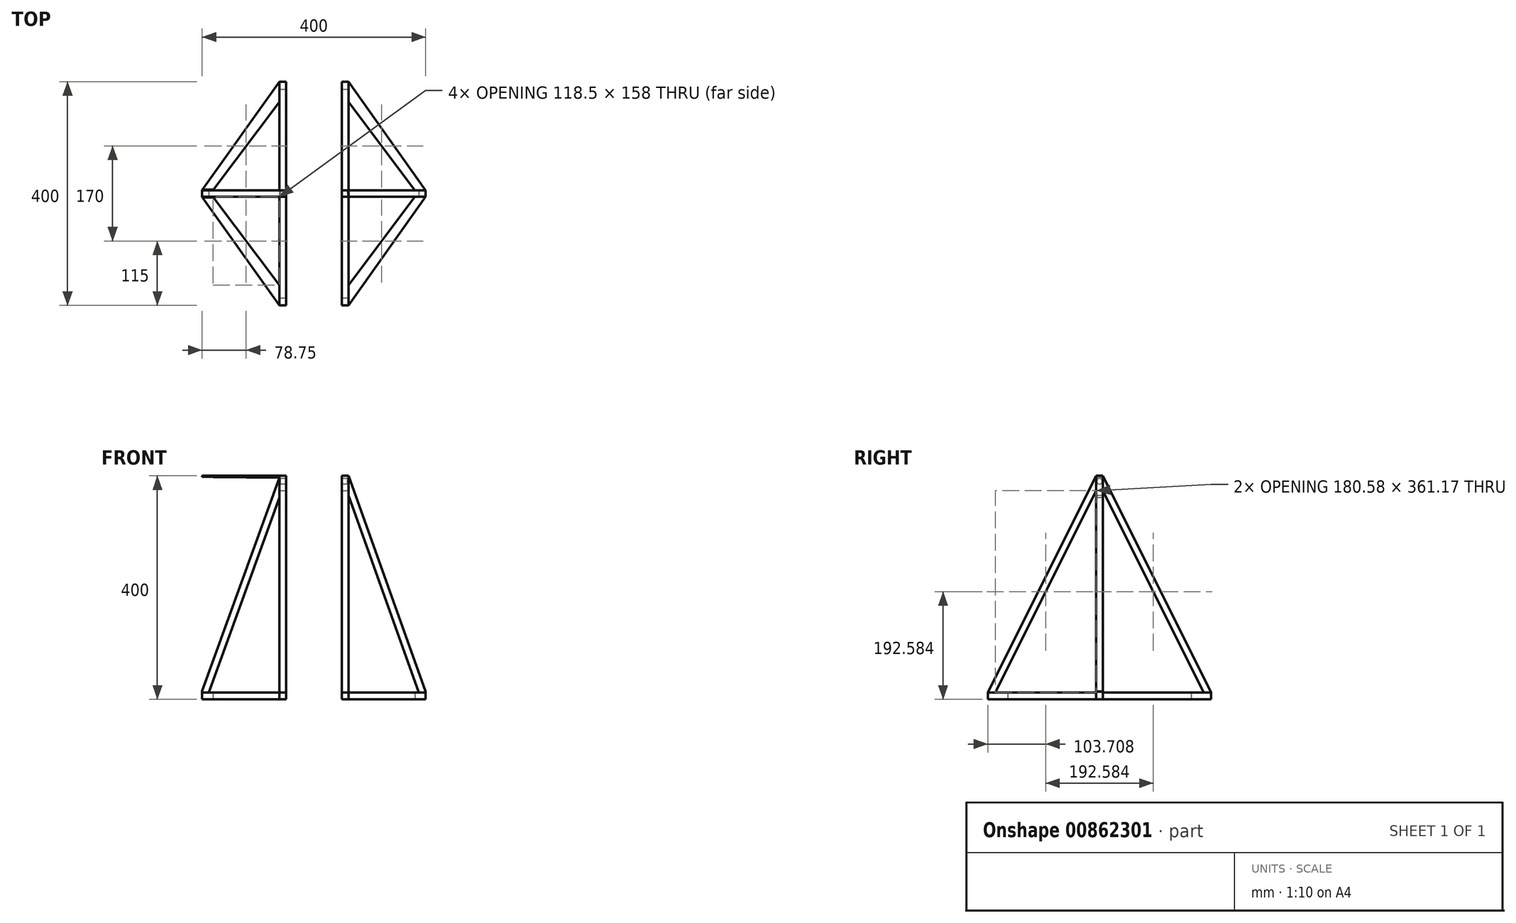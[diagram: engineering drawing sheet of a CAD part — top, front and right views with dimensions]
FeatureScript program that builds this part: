
annotation { "Feature Type Name" : "Feature", "Feature Type Description" : "" }
export const myFeature = defineFeature(function(context is Context, id is Id, definition is map)
    precondition{}
    {
        {
            var Q0;
            Q0=qCreatedBy(makeId("Top.planeOp"),FACE);
            cPlane(context, id + "F0", {"entities" : qUnion([Q0]), "cplaneType" : CPlaneType.OFFSET, "offset" : 141 * mm, "width" : 150 * mm, "height" : 150 * mm});
        }
        {
            var Q0;
            Q0=qCreatedBy(makeId("Top.planeOp"),FACE);
            var sketch = newSketch(context, id + "F1", { "sketchPlane" : qUnion([Q0])});
            skLineSegment(sketch, "E0.bottom", {"start": v(-40, 200) * mm, "end": v(40, 200) * mm, "construction": true});
            skLineSegment(sketch, "E0.top", {"start": v(-40, -200) * mm, "end": v(40, -200) * mm, "construction": true});
            skPoint(sketch, "E0.middle", {"position": v(0, 0) * mm});
            skLineSegment(sketch, "E1", {"start": v(-200, 0) * mm, "end": v(200, 0) * mm, "construction": true});
            skLineSegment(sketch, "E2.bottom", {"start": v(-50, 200) * mm, "end": v(50, 200) * mm, "construction": true});
            skLineSegment(sketch, "E2.top", {"start": v(-50, -200) * mm, "end": v(50, -200) * mm, "construction": true});
            skLineSegment(sketch, "E2.left", {"start": v(-50, 200) * mm, "end": v(-50, -200) * mm, "construction": true});
            skLineSegment(sketch, "E2.right", {"start": v(50, 200) * mm, "end": v(50, -200) * mm, "construction": true});
            skLineSegment(sketch, "E3.bottom", {"start": v(-200, 6) * mm, "end": v(200, 6) * mm, "construction": true});
            skLineSegment(sketch, "E3.top", {"start": v(-200, -6) * mm, "end": v(200, -6) * mm, "construction": true});
            skLineSegment(sketch, "E3.left", {"start": v(-200, 6) * mm, "end": v(-200, -6) * mm, "construction": true});
            skLineSegment(sketch, "E3.right", {"start": v(200, 6) * mm, "end": v(200, -6) * mm, "construction": true});
            skLineSegment(sketch, "E4", {"start": v(-200, 6) * mm, "end": v(-200, -6) * mm});
            skLineSegment(sketch, "E5.bottom", {"start": v(-50, 200) * mm, "end": v(-62, 200) * mm, "construction": true});
            skLineSegment(sketch, "E5.top", {"start": v(-50, -200) * mm, "end": v(-62, -200) * mm, "construction": true});
            skLineSegment(sketch, "E5.right", {"start": v(-62, 200) * mm, "end": v(-62, -200) * mm, "construction": true});
            skLineSegment(sketch, "E6", {"start": v(0, -95.75) * mm, "end": v(0, 160.13) * mm, "construction": true});
            skPoint(sketch, "E6.endSnap0", {"position": v(0, -6) * mm});
            skLineSegment(sketch, "E7.bottom", {"start": v(50, 200) * mm, "end": v(62, 200) * mm, "construction": true});
            skLineSegment(sketch, "E7.top", {"start": v(50, -200) * mm, "end": v(62, -200) * mm, "construction": true});
            skLineSegment(sketch, "E7.right", {"start": v(62, 200) * mm, "end": v(62, -200) * mm, "construction": true});
            skLineSegment(sketch, "E8", {"start": v(-62, 200) * mm, "end": v(-200, 6) * mm});
            skLineSegment(sketch, "E9", {"start": v(-62, 200) * mm, "end": v(-50, 200) * mm});
            skLineSegment(sketch, "E10", {"start": v(-50, 200) * mm, "end": v(-50, -200) * mm});
            skLineSegment(sketch, "E11", {"start": v(-50, -200) * mm, "end": v(-62, -200) * mm});
            skLineSegment(sketch, "E12", {"start": v(-62, -200) * mm, "end": v(-200, -6) * mm});
            skLineSegment(sketch, "E13", {"start": v(50, 200) * mm, "end": v(62, 200) * mm});
            skLineSegment(sketch, "E14", {"start": v(62, 200) * mm, "end": v(200, 6) * mm});
            skLineSegment(sketch, "E15", {"start": v(200, 6) * mm, "end": v(200, -6) * mm});
            skLineSegment(sketch, "E16", {"start": v(200, -6) * mm, "end": v(62, -200) * mm});
            skLineSegment(sketch, "E17", {"start": v(62, -200) * mm, "end": v(50, -200) * mm});
            skLineSegment(sketch, "E18", {"start": v(50, -200) * mm, "end": v(50, 200) * mm});
            skSolve(sketch);
        }
        {
            var Q0;
            Q0 = qSketchRegion(id + "F1", true);
            extrude(context, id + "F2", {"entities" : qUnion([Q0]), "depth" : 400 * mm, "offsetDistance" : 25 * mm});
        }
        {
            var Q0;
            Q0=qCreatedBy(makeId("Front.planeOp"),FACE);
            var sketch = newSketch(context, id + "F3", { "sketchPlane" : qUnion([Q0])});
            skLineSegment(sketch, "E19.bottom", {"start": v(50, 0) * mm, "end": v(-50, 0) * mm, "construction": true});
            skLineSegment(sketch, "E19.top", {"start": v(50, 400) * mm, "end": v(-48.58, 400) * mm, "construction": true});
            skLineSegment(sketch, "E20", {"start": v(-200, 15) * mm, "end": v(-62, 396.08) * mm});
            skLineSegment(sketch, "E21", {"start": v(-62, 360.83) * mm, "end": v(-188.32, 12) * mm});
            skLineSegment(sketch, "E22", {"start": v(-188.32, 12) * mm, "end": v(-62, 12) * mm});
            skLineSegment(sketch, "E23", {"start": v(-62, 12) * mm, "end": v(-62, 360.83) * mm});
            skLineSegment(sketch, "E24.bottom", {"start": v(-50, 0) * mm, "end": v(-340.13, 0) * mm, "construction": true});
            skLineSegment(sketch, "E24.top", {"start": v(-50, 400) * mm, "end": v(-340.13, 400) * mm, "construction": true});
            skLineSegment(sketch, "E24.left", {"start": v(-50, 0) * mm, "end": v(-50, 400) * mm, "construction": true});
            skLineSegment(sketch, "E24.right", {"start": v(-340.13, 0) * mm, "end": v(-340.13, 400) * mm, "construction": true});
            skLineSegment(sketch, "E25", {"start": v(-62, 396.08) * mm, "end": v(-340.13, 400) * mm});
            skLineSegment(sketch, "E26", {"start": v(-340.13, 400) * mm, "end": v(-200, 15) * mm});
            skLineSegment(sketch, "E27.left", {"start": v(50, 0) * mm, "end": v(50, 400) * mm, "construction": true});
            skSolve(sketch);
        }
        {
            var Q0;
            Q0 = qSketchRegion(id + "F3", true);
            extrude(context, id + "F4", {"entities" : qUnion([Q0]), "operationType" : NewBodyOperationType.REMOVE, "endBound" : BoundingType.SYMMETRIC, "oppositeDirection" : true, "depth" : 1000 * mm, "offsetDistance" : 25 * mm});
        }
        {
            var Q0;
            Q0=qCreatedBy(makeId("Front.planeOp"),FACE);
            var sketch = newSketch(context, id + "F5", { "sketchPlane" : qUnion([Q0])});
            skLineSegment(sketch, "E28.bottom", {"start": v(50, 0) * mm, "end": v(-50, 0) * mm, "construction": true});
            skLineSegment(sketch, "E28.top", {"start": v(50, 400) * mm, "end": v(-50, 400) * mm, "construction": true});
            skLineSegment(sketch, "E28.left", {"start": v(50, 0) * mm, "end": v(50, 400) * mm, "construction": true});
            skLineSegment(sketch, "E28.right", {"start": v(-50, 0) * mm, "end": v(-50, 400) * mm, "construction": true});
            skLineSegment(sketch, "E29.bottom", {"start": v(50, 0) * mm, "end": v(200, 0) * mm, "construction": true});
            skLineSegment(sketch, "E30", {"start": v(62, 364.36) * mm, "end": v(62, 12) * mm});
            skLineSegment(sketch, "E31", {"start": v(188, 12) * mm, "end": v(62, 364.36) * mm});
            skLineSegment(sketch, "E32", {"start": v(62, 12) * mm, "end": v(188, 12) * mm});
            skLineSegment(sketch, "E33", {"start": v(62, 400) * mm, "end": v(200, 14.08) * mm});
            skLineSegment(sketch, "E34", {"start": v(200, 14.08) * mm, "end": v(200, 400) * mm});
            skLineSegment(sketch, "E35", {"start": v(62, 400) * mm, "end": v(200, 400) * mm});
            skSolve(sketch);
        }
        {
            var Q0;
            Q0 = qSketchRegion(id + "F5", true);
            extrude(context, id + "F6", {"entities" : qUnion([Q0]), "operationType" : NewBodyOperationType.REMOVE, "endBound" : BoundingType.SYMMETRIC, "oppositeDirection" : true, "depth" : 1000 * mm, "offsetDistance" : 25 * mm});
        }
        {
            var Q0;
            Q0=qCreatedBy(makeId("Right.planeOp"),FACE);
            var sketch = newSketch(context, id + "F7", { "sketchPlane" : qUnion([Q0])});
            skLineSegment(sketch, "E36.bottom", {"start": v(200, 0) * mm, "end": v(-200, 0) * mm, "construction": true});
            skLineSegment(sketch, "E36.top", {"start": v(200, 400) * mm, "end": v(-200, 400) * mm, "construction": true});
            skLineSegment(sketch, "E36.left", {"start": v(200, 0) * mm, "end": v(200, 400) * mm, "construction": true});
            skLineSegment(sketch, "E36.right", {"start": v(-200, 0) * mm, "end": v(-200, 400) * mm, "construction": true});
            skLineSegment(sketch, "E37", {"start": v(-200, 400) * mm, "end": v(-200, 12) * mm});
            skLineSegment(sketch, "E38", {"start": v(-200, 12) * mm, "end": v(-6, 400) * mm});
            skLineSegment(sketch, "E39", {"start": v(-6, 400) * mm, "end": v(-200, 400) * mm});
            skLineSegment(sketch, "E40", {"start": v(0, 0) * mm, "end": v(0, 400) * mm, "construction": true});
            skLineSegment(sketch, "E41", {"start": v(200, 400) * mm, "end": v(200, 12) * mm});
            skLineSegment(sketch, "E42", {"start": v(200, 12) * mm, "end": v(6, 400) * mm});
            skLineSegment(sketch, "E43", {"start": v(6, 400) * mm, "end": v(200, 400) * mm});
            skLineSegment(sketch, "E44.bottom", {"start": v(-200, 0) * mm, "end": v(200, 0) * mm, "construction": true});
            skLineSegment(sketch, "E44.top", {"start": v(-200, 12) * mm, "end": v(200, 12) * mm, "construction": true});
            skLineSegment(sketch, "E44.left", {"start": v(-200, 0) * mm, "end": v(-200, 12) * mm, "construction": true});
            skLineSegment(sketch, "E44.right", {"start": v(200, 0) * mm, "end": v(200, 12) * mm, "construction": true});
            skLineSegment(sketch, "E45", {"start": v(-186.58, 12) * mm, "end": v(-6, 373.17) * mm});
            skLineSegment(sketch, "E46", {"start": v(-6, 373.17) * mm, "end": v(-6, 12) * mm});
            skLineSegment(sketch, "E47", {"start": v(-6, 12) * mm, "end": v(-186.58, 12) * mm});
            skLineSegment(sketch, "E48", {"start": v(186.58, 12) * mm, "end": v(6, 373.17) * mm});
            skLineSegment(sketch, "E49", {"start": v(6, 373.17) * mm, "end": v(6, 12) * mm});
            skLineSegment(sketch, "E50", {"start": v(6, 12) * mm, "end": v(186.58, 12) * mm});
            skSolve(sketch);
        }
        {
            var Q0;
            Q0 = qSketchRegion(id + "F7", true);
            extrude(context, id + "F8", {"entities" : qUnion([Q0]), "operationType" : NewBodyOperationType.REMOVE, "endBound" : BoundingType.SYMMETRIC, "oppositeDirection" : true, "depth" : 400 * mm, "offsetDistance" : 25 * mm});
        }
        {
            var Q0;
            Q0=qCreatedBy(makeId("Top.planeOp"),FACE);
            var sketch = newSketch(context, id + "F9", { "sketchPlane" : qUnion([Q0])});
            skLineSegment(sketch, "E51.bottom", {"start": v(-50, 200) * mm, "end": v(50, 200) * mm, "construction": true});
            skLineSegment(sketch, "E51.top", {"start": v(-50, -200) * mm, "end": v(50, -200) * mm, "construction": true});
            skLineSegment(sketch, "E51.left", {"start": v(-50, 200) * mm, "end": v(-50, -200) * mm, "construction": true});
            skLineSegment(sketch, "E51.right", {"start": v(50, 200) * mm, "end": v(50, -200) * mm, "construction": true});
            skPoint(sketch, "E51.middle", {"position": v(0, 0) * mm});
            skLineSegment(sketch, "E52", {"start": v(0, 0) * mm, "end": v(200, 0) * mm, "construction": true});
            skLineSegment(sketch, "E53", {"start": v(50, 200) * mm, "end": v(200, 0) * mm, "construction": true});
            skLineSegment(sketch, "E54", {"start": v(50, 200) * mm, "end": v(50, 0) * mm, "construction": true});
            skLineSegment(sketch, "E55", {"start": v(180.5, 6) * mm, "end": v(62, 164) * mm});
            skLineSegment(sketch, "E56", {"start": v(62, 164) * mm, "end": v(62, 6) * mm});
            skLineSegment(sketch, "E57", {"start": v(62, 6) * mm, "end": v(180.5, 6) * mm});
            skLineSegment(sketch, "E58", {"start": v(50, -200) * mm, "end": v(200, 0) * mm, "construction": true});
            skLineSegment(sketch, "E59", {"start": v(62, -6) * mm, "end": v(62, -164) * mm});
            skLineSegment(sketch, "E60", {"start": v(62, -164) * mm, "end": v(180.5, -6) * mm});
            skLineSegment(sketch, "E61", {"start": v(180.5, -6) * mm, "end": v(62, -6) * mm});
            skLineSegment(sketch, "E62", {"start": v(0, 0) * mm, "end": v(0, 210) * mm, "construction": true});
            skLineSegment(sketch, "E63", {"start": v(-62, 164) * mm, "end": v(-62, 6) * mm});
            skLineSegment(sketch, "E64", {"start": v(-62, 6) * mm, "end": v(-180.5, 6) * mm});
            skLineSegment(sketch, "E65", {"start": v(-180.5, 6) * mm, "end": v(-62, 164) * mm});
            skLineSegment(sketch, "E66", {"start": v(-180.5, -6) * mm, "end": v(-62, -6) * mm});
            skLineSegment(sketch, "E67", {"start": v(-62, -6) * mm, "end": v(-62, -164) * mm});
            skLineSegment(sketch, "E68", {"start": v(-62, -164) * mm, "end": v(-180.5, -6) * mm});
            skSolve(sketch);
        }
        {
            var Q0;
            Q0 = qSketchRegion(id + "F9", true);
            extrude(context, id + "F10", {"entities" : qUnion([Q0]), "operationType" : NewBodyOperationType.REMOVE, "depth" : 400 * mm, "offsetDistance" : 25 * mm});
        }
        {
            var Q0;
            Q0=qCreatedBy(makeId("Right.planeOp"),FACE);
            var sketch = newSketch(context, id + "F11", { "sketchPlane" : qUnion([Q0])});
            skLineSegment(sketch, "E69", {"start": v(0, 0) * mm, "end": v(0, 390) * mm, "construction": true});
            skCircle(sketch, "E70", {"center": v(0, 390) * mm, "radius": 5 * mm});
            skSolve(sketch);
        }
        {
            var Q0;
            Q0 = qSketchRegion(id + "F11", true);
            extrude(context, id + "F12", {"entities" : qUnion([Q0]), "operationType" : NewBodyOperationType.REMOVE, "endBound" : BoundingType.SYMMETRIC, "depth" : 120 * mm, "offsetDistance" : 25 * mm});
        }
        {
            var Q0;
            Q0=qCreatedBy(id+"F0.planeOp",FACE);
            var sketch = newSketch(context, id + "F13", { "sketchPlane" : qUnion([Q0])});
            skLineSegment(sketch, "E71.bottom", {"start": v(-200, 6) * mm, "end": v(200, 6) * mm, "construction": true});
            skLineSegment(sketch, "E71.top", {"start": v(-200, -6) * mm, "end": v(200, -6) * mm, "construction": true});
            skLineSegment(sketch, "E71.left", {"start": v(-200, 6) * mm, "end": v(-200, -6) * mm, "construction": true});
            skLineSegment(sketch, "E71.right", {"start": v(200, 6) * mm, "end": v(200, -6) * mm, "construction": true});
            skPoint(sketch, "E71.middle", {"position": v(0, 0) * mm});
            skLineSegment(sketch, "E72.bottom", {"start": v(-62, 200) * mm, "end": v(62, 200) * mm, "construction": true});
            skLineSegment(sketch, "E72.top", {"start": v(-62, -200) * mm, "end": v(62, -200) * mm, "construction": true});
            skLineSegment(sketch, "E72.left", {"start": v(-62, 200) * mm, "end": v(-62, -200) * mm, "construction": true});
            skLineSegment(sketch, "E72.right", {"start": v(62, 200) * mm, "end": v(62, -200) * mm, "construction": true});
            skLineSegment(sketch, "E73", {"start": v(-62, -6) * mm, "end": v(-200, -6) * mm});
            skLineSegment(sketch, "E74", {"start": v(-200, -6) * mm, "end": v(-62, -200) * mm});
            skLineSegment(sketch, "E75", {"start": v(-62, -200) * mm, "end": v(-62, -6) * mm});
            skLineSegment(sketch, "E76", {"start": v(-62, 6) * mm, "end": v(-62, 200) * mm});
            skLineSegment(sketch, "E77", {"start": v(-62, 6) * mm, "end": v(-200, 6) * mm});
            skLineSegment(sketch, "E78", {"start": v(-200, 6) * mm, "end": v(-62, 200) * mm});
            skLineSegment(sketch, "E79", {"start": v(62, 6) * mm, "end": v(200, 6) * mm});
            skLineSegment(sketch, "E80", {"start": v(62, 6) * mm, "end": v(62, 200) * mm});
            skLineSegment(sketch, "E81", {"start": v(62, 200) * mm, "end": v(200, 6) * mm});
            skLineSegment(sketch, "E82", {"start": v(62, -6) * mm, "end": v(62, -200) * mm});
            skLineSegment(sketch, "E83", {"start": v(62, -6) * mm, "end": v(200, -6) * mm});
            skLineSegment(sketch, "E84", {"start": v(200, -6) * mm, "end": v(62, -200) * mm});
            skSolve(sketch);
        }
        {
            var Q0;
            Q0 = qSketchRegion(id + "F13", true);
            extrude(context, id + "F14", {"entities" : qUnion([Q0]), "operationType" : NewBodyOperationType.REMOVE, "depth" : 106 * mm, "offsetDistance" : 25 * mm});
        }
    });
